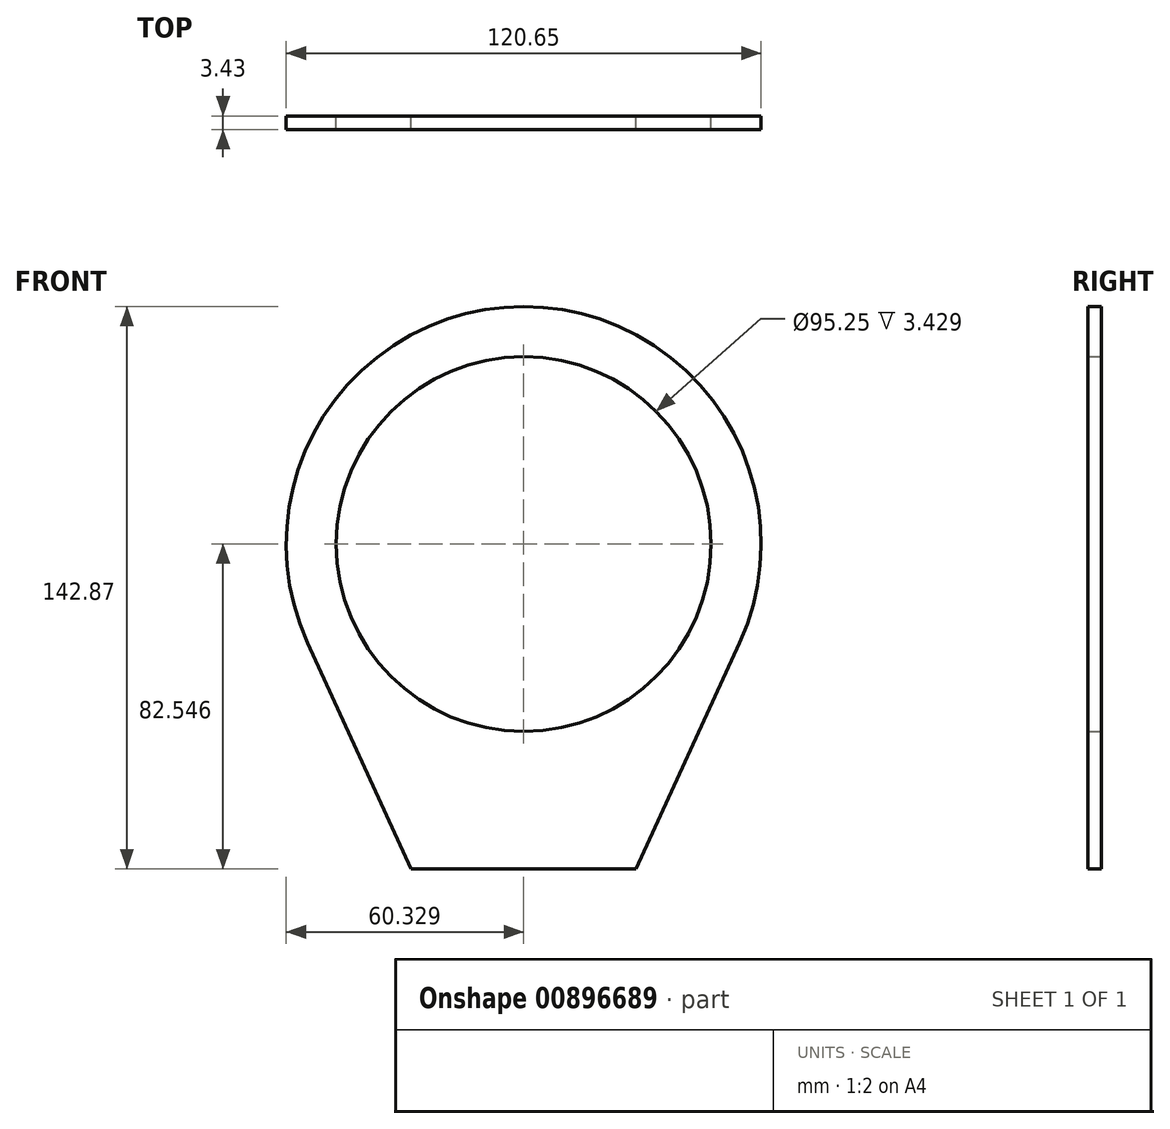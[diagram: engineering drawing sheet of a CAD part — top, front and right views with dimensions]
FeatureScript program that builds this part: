
annotation { "Feature Type Name" : "Feature", "Feature Type Description" : "" }
export const myFeature = defineFeature(function(context is Context, id is Id, definition is map)
    precondition{}
    {
        {
            var Q0;
            Q0=qCreatedBy(makeId("Front.planeOp"),FACE);
            var sketch = newSketch(context, id + "F0", { "sketchPlane" : qUnion([Q0])});
            skCircle(sketch, "E0", {"center": v(-181.08, 529.13) * mm, "radius": 47.63 * mm});
            skLineSegment(sketch, "E1", {"start": v(-209.66, 446.58) * mm, "end": v(-152.5, 446.58) * mm});
            skLineSegment(sketch, "E2", {"start": v(-235.94, 504.03) * mm, "end": v(-209.66, 446.58) * mm});
            skArc(sketch, "E3", {"start": v(-126.22, 504.03) * mm, "mid": v(-181.08, 589.45) * mm, "end": v(-235.94, 504.03) * mm});
            skLineSegment(sketch, "E4", {"start": v(-152.5, 446.58) * mm, "end": v(-126.22, 504.03) * mm});
            skSolve(sketch);
        }
        {
            var Q0;
            Q0 = qSketchRegion(id + "F0", true);
            extrude(context, id + "F1", {"entities" : qUnion([Q0]), "depth" : 3.43 * mm, "offsetDistance" : 25.4 * mm});
        }
    });
